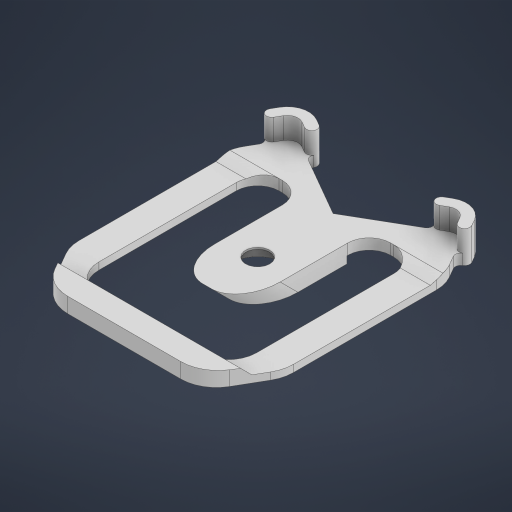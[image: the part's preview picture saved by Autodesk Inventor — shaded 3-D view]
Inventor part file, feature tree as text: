
AUTODESK INVENTOR PART (.ipt)
format: ipt  version: 2023 (Build 270158000, 158)  size: 450,048 bytes
history: native  units: in
note: dims shown in document units (in); Inventor stores cm internally (conversion verified against a paired STEP export)
features: extrude x7, chamfer x4, sketch x2, fillet x2, draft x1
ambient origin geometry x8: Origin, YZ Plane, XZ Plane, XY Plane, X Axis, Y Axis, Z Axis, Center Point
bodies: Solid1 (feature_tree)
feature tree (16):
  extrude  "Extrusion1"  Depth=0.1181in
  extrude  "Extrusion2"  Depth=0.1969in TaperAngle=0.0deg
  extrude  "Extrusion3"  Depth=0.0197in
  extrude  "Extrusion4"  Depth=0.1181in
  extrude  "Extrusion5"  Depth=0.315in
  chamfer  "Chamfer1"  Distance=0.2362in
  chamfer  "Chamfer2"  Distance=0.2362in
  chamfer  "Chamfer3"  Distance=0.5689in
  sketch  "Sketch2"  dims[d1=0.374in d3=120.0deg d4=60.0deg d5=0.1772in d6=2.9528in d11=0.0886in d14=60.0deg d15=0.1772in d16=0.0886in d17=1.5748in d18=0.1181in]
  fillet  "Fillet3"  Radius=0.0787in
  extrude  "Extrusion7"  Depth=0.0787in
  draft  "FaceDraft3"
  fillet  "Fillet10"  Radius=0.0787in
  chamfer  "Chamfer8"  Distance=0.0197in
  extrude  "Extrusion10"  Depth=0.0394in TaperAngle=0.0deg
  sketch  "Sketch7"  dims[d19=0.3937in d20=0.1969in d21=0.0in d22=0.2657in d24=0.1181in d25=0.315in d26=0.2362in d27=0.2362in d28=0.5689in d29=0.0787in d30=0.0787in d31=0.0787in d32=0.0197in d33=0.0in d34=0.0394in d35=0.0in d36=0.2362in d37=0.0in d38=0.0in d39=0.0in d40=0.0in d41=0.0in d42=0.0591in d43=0.2362in d44=0.0in d45=0.2756in d46=0.0492in d47=0.0in d48=0.2756in d49=0.0098in d50=45.0deg d52=0.0394in d53=0.1575in d54=75.0deg d55=0.0394in d56=0.1575in d57=75.0deg d66=0.315in d67=0.3937in d72=0.1575in d73=0.0in d74=45.0deg d105=0.315in d106=0.0787in d107=0.0787in d108=0.2405in d109=0.0787in d110=0.0in d51=0.0in d59=0.0in d60=0.0in d61=0.0in d62=0.0in d63=0.0in d64=0.0in d65=0.0in d68=0.0344in d69=0.0197in d70=0.0344in d104=0.0in]
